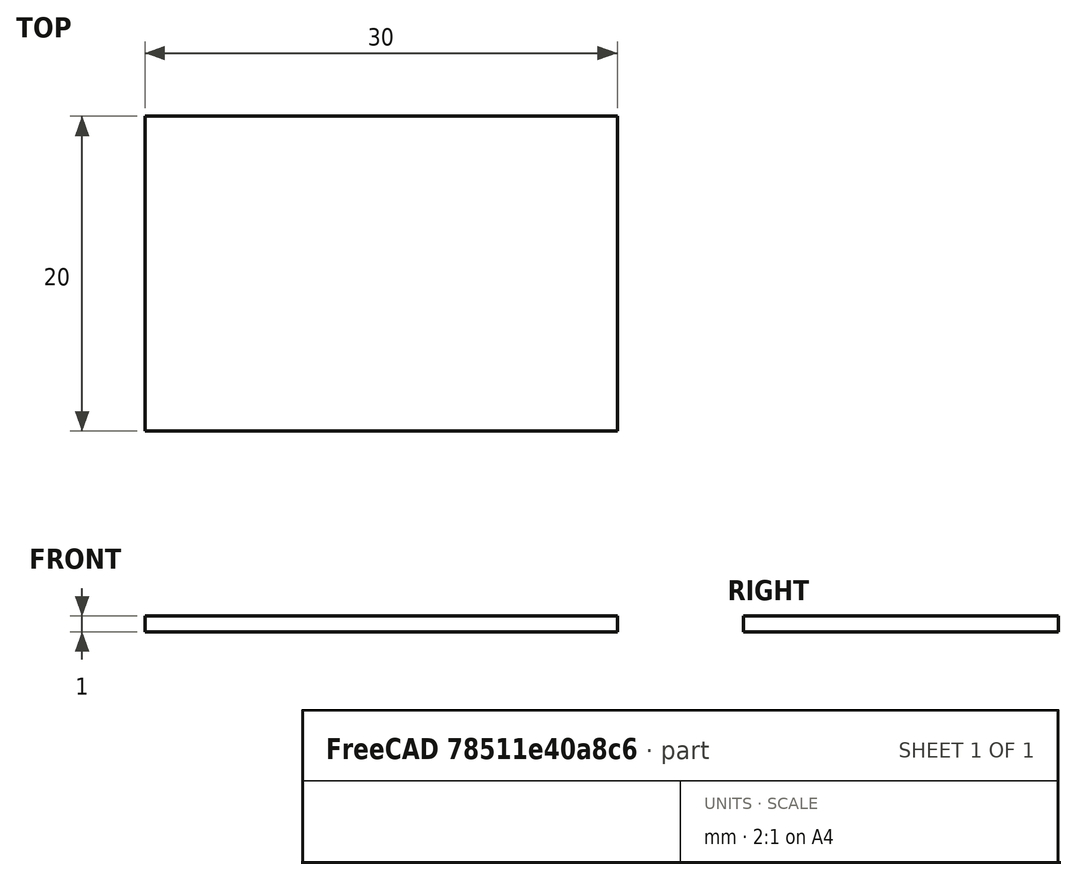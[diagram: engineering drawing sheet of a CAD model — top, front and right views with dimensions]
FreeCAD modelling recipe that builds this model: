
FCSTD DOCUMENT  (FreeCAD 1.0R39285 (Git))
Label: boiteMusique_tambour
License: All rights reserved
LicenseURL: https://en.wikipedia.org/wiki/All_rights_reserved
objects: Sketcher::SketchObject×2, PartDesign::Pad×1, PartDesign::Body×1, Spreadsheet::Sheet×1
note: 8 computed .brp shape members not serialized (recipe doc carries the construction recipe); baked Part::Feature solids carry a one-line shape summary decoded from their .brp

FEATURE [Sketcher::SketchObject] Sketch
  ArcFitTolerance = 1e-06
  AttachmentSupport = -> [XY_Plane]
  FullyConstrained = true
  MakeInternals = false
  MapMode = 5
  sketch-geometry (4):
    g0: LineSegment StartX=0 StartY=0 StartZ=0 EndX=30 EndY=0 EndZ=0
    g1: LineSegment StartX=30 StartY=0 StartZ=0 EndX=30 EndY=20 EndZ=0
    g2: LineSegment StartX=30 StartY=20 StartZ=0 EndX=0 EndY=20 EndZ=0
    g3: LineSegment StartX=0 StartY=20 StartZ=0 EndX=0 EndY=0 EndZ=0
  constraints (11):
    c: Coincident(g0,g1)
    c: Coincident(g1,g2)
    c: Coincident(g2,g3)
    c: Coincident(g3,g0)
    c: Horizontal(g0)
    c: Horizontal(g2)
    c: Vertical(g1)
    c: Vertical(g3)
    c: Coincident(g0,g-1)
    c: DistanceX(g0,g0) = 30
    c: DistanceY(g3,g3) = 20
FEATURE [PartDesign::Pad] Pad
  Direction = (0,0,1)
  Length = 1
  Length2 = 10
  Profile = -> Sketch
  ReferenceAxis = -> Sketch [N_Axis]
  Reversed = true
  Suppressed = false
  Type = 0
FEATURE [Sketcher::SketchObject] Sketch001
  ArcFitTolerance = 1e-06
  AttachmentSupport = -> [Pad]
  ExternalGeometry = -> [Pad]
  FullyConstrained = false
  MakeInternals = false
  MapMode = 5
  sketch-geometry (1):
    g0: LineSegment [constr] StartX=2.84675 StartY=20 StartZ=0 EndX=2.84675 EndY=0 EndZ=0
  constraints (3):
    c: PointOnObject(g0,g-3)
    c: PointOnObject(g0,g-4)
    c: Vertical(g0)
FEATURE [PartDesign::Body] Body
  AllowCompound = false
  Group = -> [Sketch,Pad,Sketch001]
  Origin = -> Origin
  Tip = -> Pad
FEATURE [Spreadsheet::Sheet] Spreadsheet
  cells = A1='tambour_largeur; B1(tambour_largeur)==20 mm; A2='tambour_longueur; B2(tambour_longueur)==30 mm; A3='tambour_epaisseur; B3(tambour_epaisseur)==1 mm; A4='note_tempo; B4(note_tempo)==1 mm; A5='note_spacing; B5(note_spacing)==1.5 mm; A6='note_hauteur; B6(note_hauteur)==1 mm; A7='note_largeur; B7(note_largeur)==1 mm; A8='note_longueur; B8(note_longueur)==1 mm
